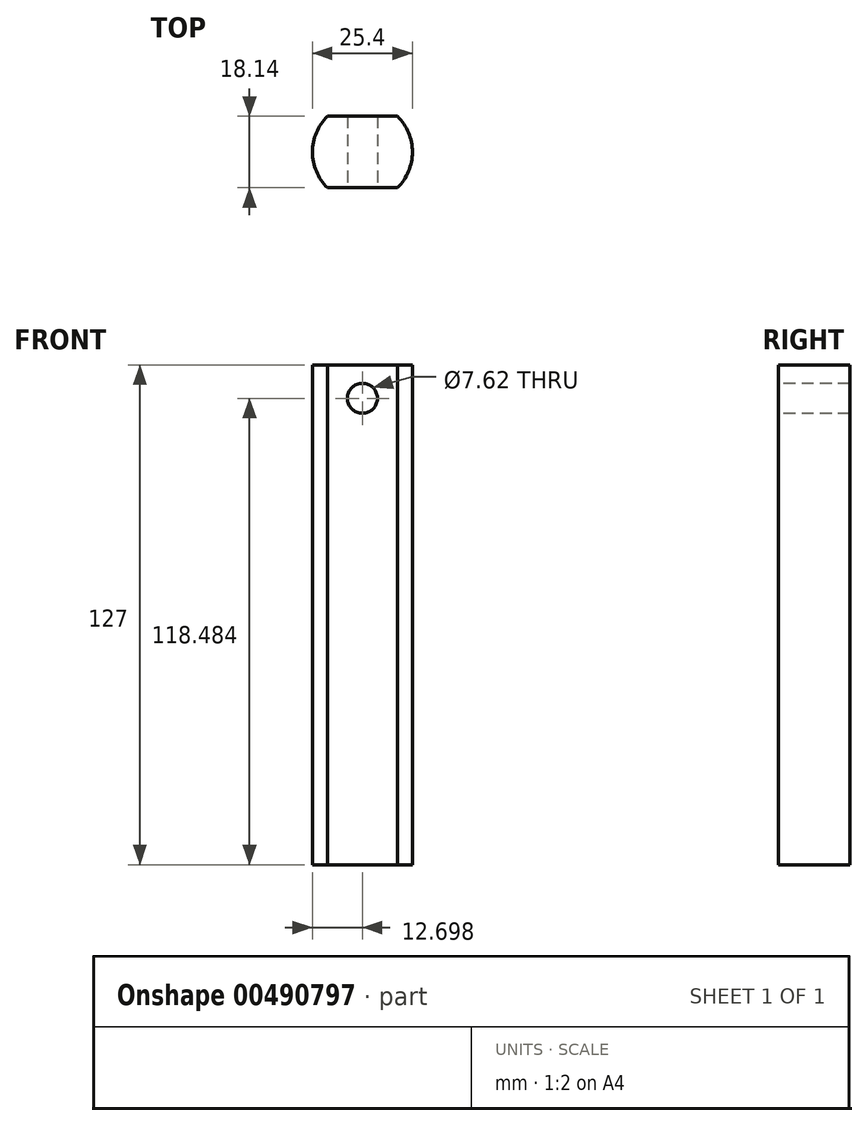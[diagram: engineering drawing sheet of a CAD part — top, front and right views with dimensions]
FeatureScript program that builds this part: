
annotation { "Feature Type Name" : "Feature", "Feature Type Description" : "" }
export const myFeature = defineFeature(function(context is Context, id is Id, definition is map)
    precondition{}
    {
        {
            var Q0;
            Q0=qCreatedBy(makeId("Top.planeOp"),FACE);
            var sketch = newSketch(context, id + "F0", { "sketchPlane" : qUnion([Q0])});
            skArc(sketch, "E0", {"start": v(-52.06, -34.78) * mm, "mid": v(-48.25, -25.71) * mm, "end": v(-52.06, -16.64) * mm});
            skLineSegment(sketch, "E1", {"start": v(-69.84, -34.78) * mm, "end": v(-52.06, -34.78) * mm});
            skLineSegment(sketch, "E2", {"start": v(-69.84, -16.64) * mm, "end": v(-52.06, -16.64) * mm});
            skArc(sketch, "E3.trimOffspring", {"start": v(-69.84, -16.64) * mm, "mid": v(-73.65, -25.71) * mm, "end": v(-69.84, -34.78) * mm});
            skSolve(sketch);
        }
        {
            var Q0;
            Q0=qSketchRegion(id+"F0",true);
            extrude(context, id + "F1", {"entities" : qUnion([Q0]), "depth" : 127 * mm});
        }
        {
            var Q0;
            Q0=makeQuery(id+"F1.opExtrude","SWEPT_FACE",FACE,{"disambiguationData":[OSD([sQuery(id+"F0.wireOp",EDGE,"E1")])]});
            var sketch = newSketch(context, id + "F2", { "sketchPlane" : qUnion([Q0])});
            skCircle(sketch, "E4", {"center": v(-60.95, 118.48) * mm, "radius": 3.81 * mm});
            skPoint(sketch, "E4.centerSnap0", {"position": v(-60.95, 127) * mm});
            skSolve(sketch);
        }
        {
            var Q0;
            Q0=qSketchRegion(id+"F2",true);
            extrude(context, id + "F3", {"entities" : qUnion([Q0]), "operationType" : NewBodyOperationType.REMOVE, "oppositeDirection" : true, "depth" : 25.4 * mm});
        }
    });
